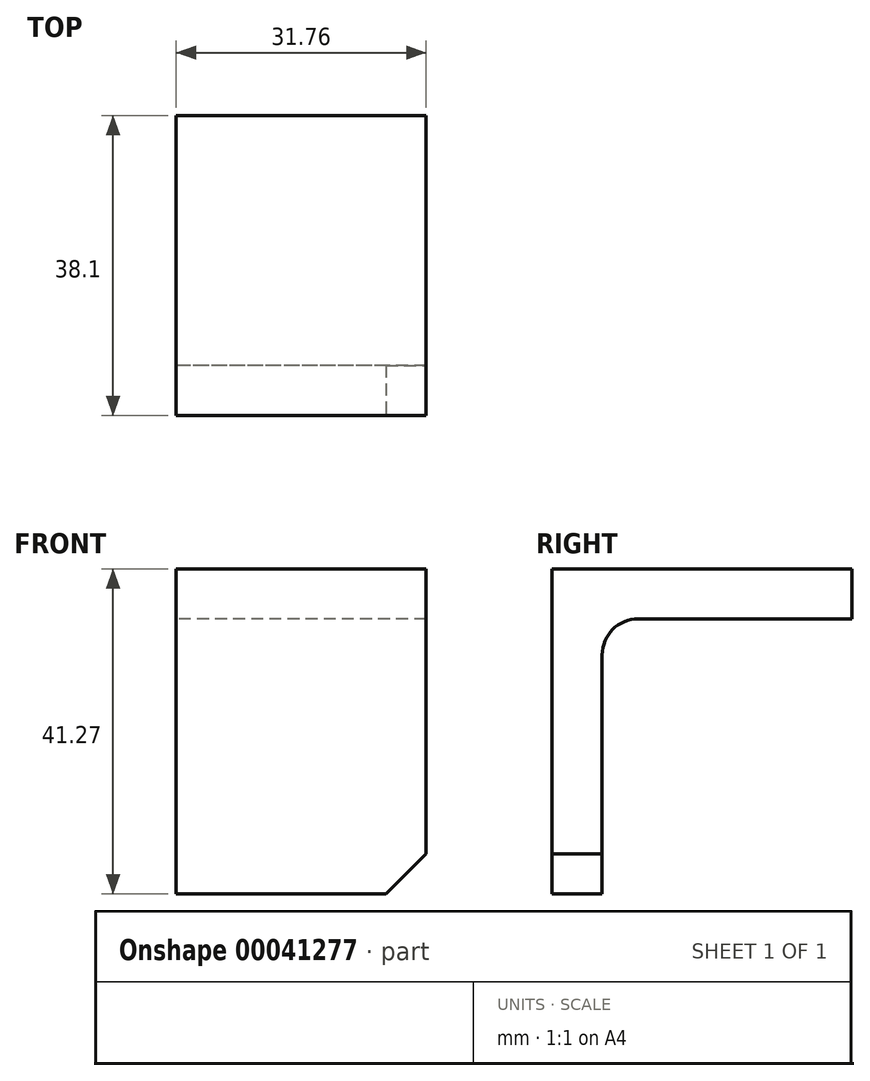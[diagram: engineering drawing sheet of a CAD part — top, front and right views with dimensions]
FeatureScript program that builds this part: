
annotation { "Feature Type Name" : "Feature", "Feature Type Description" : "" }
export const myFeature = defineFeature(function(context is Context, id is Id, definition is map)
    precondition{}
    {
        {
            var Q0;
            Q0=qCreatedBy(makeId("Right.planeOp"),FACE);
            var sketch = newSketch(context, id + "F0", { "sketchPlane" : qUnion([Q0])});
            skLineSegment(sketch, "E0", {"start": v(0, 0) * mm, "end": v(0, 41.27) * mm});
            skLineSegment(sketch, "E1", {"start": v(0, 41.28) * mm, "end": v(38.1, 41.28) * mm});
            skLineSegment(sketch, "E2", {"start": v(38.1, 41.28) * mm, "end": v(38.1, 34.93) * mm});
            skLineSegment(sketch, "E3", {"start": v(38.1, 34.93) * mm, "end": v(6.35, 34.93) * mm});
            skLineSegment(sketch, "E4", {"start": v(6.35, 34.93) * mm, "end": v(6.35, 0) * mm});
            skLineSegment(sketch, "E5", {"start": v(6.35, 0) * mm, "end": v(0, 0) * mm});
            skSolve(sketch);
        }
        {
            var Q0;
            Q0=makeQuery(id+"F0.imprint","IMPRINT",FACE,{"disambiguationData":[TD([[makeQuery(id+"F0.imprint","IMPRINT",EDGE,{"derivedFrom":sQuery(id+"F0.wireOp",EDGE,"E0")}),-1.0]])]});
            extrude(context, id + "F1", {"entities" : qUnion([Q0]), "depth" : 31.75 * mm, "symmetric" : true});
        }
        {
            var Q0;
            Q0=makeQuery(id+"F1.opExtrude","SWEPT_EDGE",EDGE,{"disambiguationData":[OSD([sQuery(id+"F0.wireOp",EDGE,"E3"),sQuery(id+"F0.wireOp",EDGE,"E4")])]});
            fillet(context, id + "F2", {"entities" : qUnion([Q0]), "radius" : 4.57 * mm, "tangentPropagation" : true, "allowEdgeOverflow" : false});
        }
        {
            var Q0;
            Q0=makeQuery(id+"F1.opExtrude","CAP_EDGE",EDGE,{"disambiguationData":[OSD([sQuery(id+"F0.wireOp",EDGE,"E5")])],"isStart":false});
            chamfer(context, id + "F3", {"entities" : qUnion([Q0]), "width" : 5.08 * mm, "tangentPropagation" : true});
        }
    });
